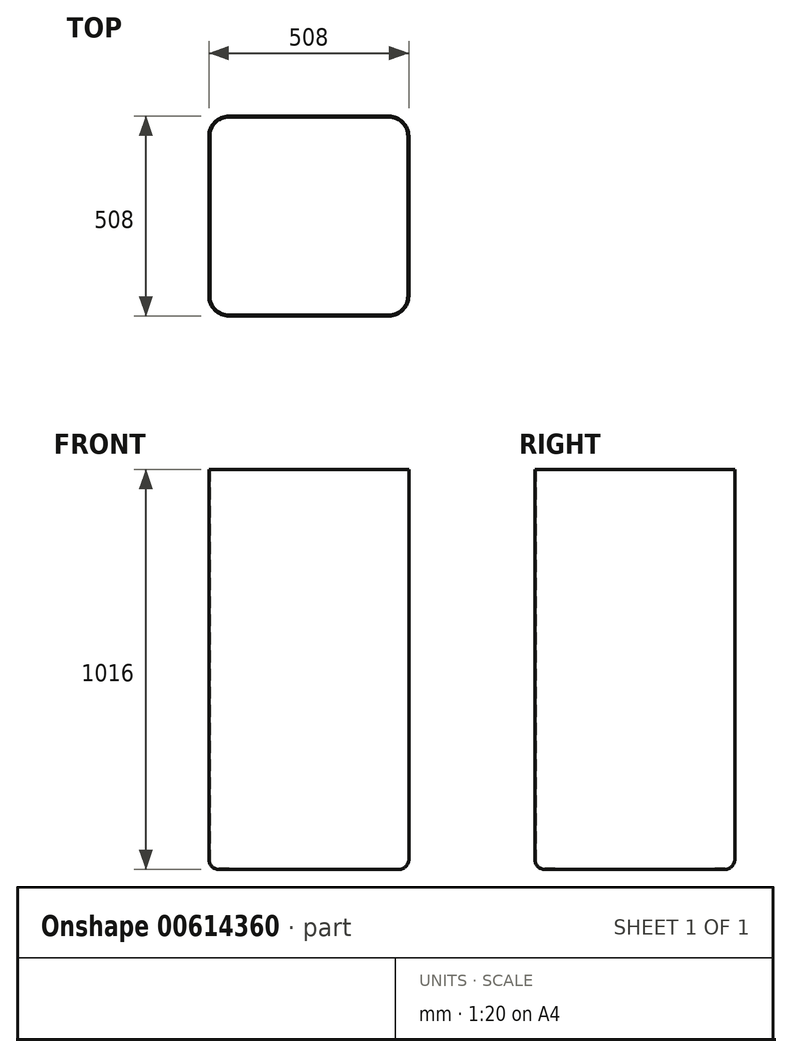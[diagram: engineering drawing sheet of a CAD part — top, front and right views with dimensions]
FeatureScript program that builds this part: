
annotation { "Feature Type Name" : "Feature", "Feature Type Description" : "" }
export const myFeature = defineFeature(function(context is Context, id is Id, definition is map)
    precondition{}
    {
        {
            var Q0;
            Q0=qCreatedBy(makeId("Top.planeOp"),FACE);
            var sketch = newSketch(context, id + "F0", { "sketchPlane" : qUnion([Q0])});
            skLineSegment(sketch, "E0", {"start": v(0, 0) * mm, "end": v(254, 0) * mm});
            skLineSegment(sketch, "E1", {"start": v(254, 0) * mm, "end": v(254, 254) * mm});
            skLineSegment(sketch, "E2.bottom", {"start": v(254, 254) * mm, "end": v(-254, 254) * mm});
            skLineSegment(sketch, "E2.top", {"start": v(254, -254) * mm, "end": v(-254, -254) * mm});
            skLineSegment(sketch, "E2.left", {"start": v(254, 254) * mm, "end": v(254, -254) * mm});
            skLineSegment(sketch, "E2.right", {"start": v(-254, 254) * mm, "end": v(-254, -254) * mm});
            skPoint(sketch, "E2.middle", {"position": v(0, 0) * mm});
            skSolve(sketch);
        }
        {
            var Q0;
            Q0=qSketchRegion(id+"F0",true);
            extrude(context, id + "F1", {"entities" : qUnion([Q0]), "depth" : 1016 * mm, "offsetDistance" : 25.4 * mm});
        }
        {
            var Q0;
            Q0=makeQuery(id+"F1.opExtrude","CAP_EDGE",EDGE,{"disambiguationData":[OSD([sQuery(id+"F0.wireOp",EDGE,"E2.right")])],"isStart":true});
            var Q1;
            Q1=makeQuery(id+"F1.opExtrude","CAP_EDGE",EDGE,{"disambiguationData":[OSD([sQuery(id+"F0.wireOp",EDGE,"E2.bottom")])],"isStart":true});
            var Q2;
            Q2=makeQuery(id+"F1.opExtrude","CAP_EDGE",EDGE,{"disambiguationData":[OSD([sQuery(id+"F0.wireOp",EDGE,"E2.top")])],"isStart":true});
            var Q3;
            Q3=makeQuery(id+"F1.opExtrude","CAP_EDGE",EDGE,{"disambiguationData":[OSD([sQuery(id+"F0.wireOp",EDGE,"E2.left")])],"isStart":true});
            fillet(context, id + "F2", {"entities" : qUnion([Q0, Q1, Q2, Q3]), "radius" : 25.4 * mm, "tangentPropagation" : true, "allowEdgeOverflow" : false});
        }
        {
            var Q0;
            Q0=makeQuery(id+"F1.opExtrude","SWEPT_EDGE",EDGE,{"disambiguationData":[OSD([sQuery(id+"F0.wireOp",EDGE,"E2.bottom"),sQuery(id+"F0.wireOp",EDGE,"E2.right")])]});
            var Q1;
            Q1=makeQuery(id+"F1.opExtrude","SWEPT_EDGE",EDGE,{"disambiguationData":[OSD([sQuery(id+"F0.wireOp",EDGE,"E2.top"),sQuery(id+"F0.wireOp",EDGE,"E2.right")])]});
            var Q2;
            Q2=makeQuery(id+"F1.opExtrude","SWEPT_EDGE",EDGE,{"disambiguationData":[OSD([sQuery(id+"F0.wireOp",EDGE,"E2.bottom"),sQuery(id+"F0.wireOp",EDGE,"E2.left")])]});
            var Q3;
            Q3=makeQuery(id+"F1.opExtrude","SWEPT_EDGE",EDGE,{"disambiguationData":[OSD([sQuery(id+"F0.wireOp",EDGE,"E2.top"),sQuery(id+"F0.wireOp",EDGE,"E2.left")])]});
            fillet(context, id + "F3", {"entities" : qUnion([Q0, Q1, Q2, Q3]), "radius" : 50.8 * mm, "tangentPropagation" : true, "allowEdgeOverflow" : false});
        }
        {
            var Q0;
            Q0=makeQuery(id+"F1.opExtrude","CAP_FACE",FACE,{"disambiguationData":[OSD([sQuery(id+"F0.wireOp",EDGE,"E2.bottom"),sQuery(id+"F0.wireOp",EDGE,"E2.top"),sQuery(id+"F0.wireOp",EDGE,"E2.left"),sQuery(id+"F0.wireOp",EDGE,"E2.right")])],"isStart":false});
            shell(context, id + "F4", {"entities" : qUnion([Q0]), "thickness" : 2.54 * mm});
        }
    });
